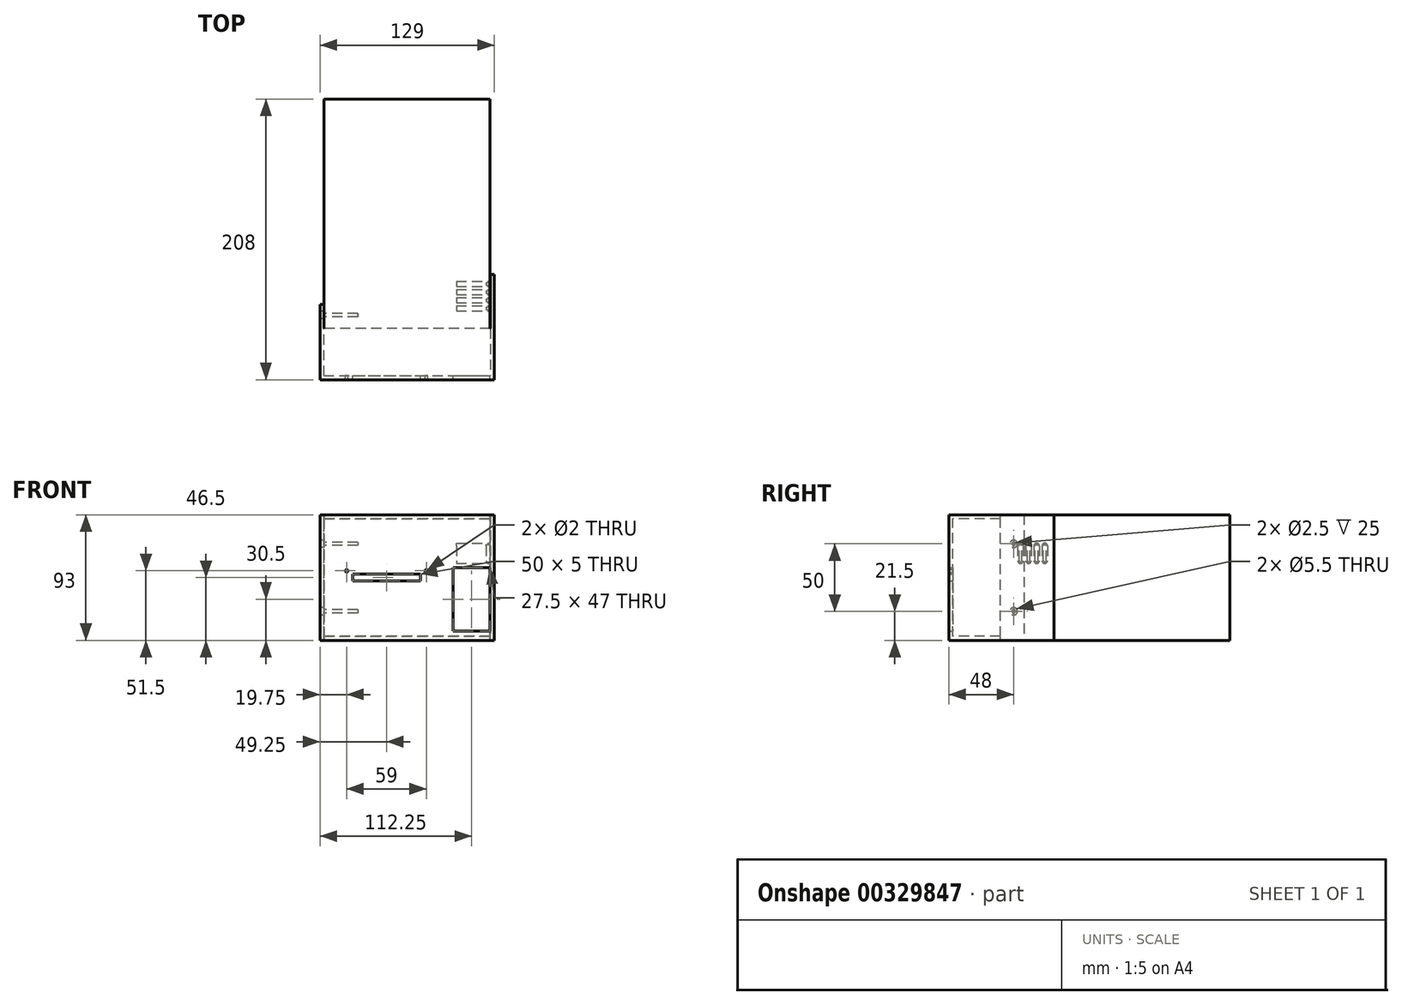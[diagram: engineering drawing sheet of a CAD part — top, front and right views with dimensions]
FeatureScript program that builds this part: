
annotation { "Feature Type Name" : "Feature", "Feature Type Description" : "" }
export const myFeature = defineFeature(function(context is Context, id is Id, definition is map)
    precondition{}
    {
        {
            assignVariable(context, id + "F0", {"name" : "CoverWallThickness", "anyValue" : 3});
        }
        {
            assignVariable(context, id + "F1", {"name" : "Gap", "anyValue" : 0.2});
        }
        {
            var Q0;
            Q0=qCreatedBy(makeId("Front.planeOp"),FACE);
            var sketch = newSketch(context, id + "F2", { "sketchPlane" : qUnion([Q0])});
            skLineSegment(sketch, "E0.bottom", {"start": v(0, 0) * mm, "end": v(123, 0) * mm});
            skLineSegment(sketch, "E0.top", {"start": v(0, 93) * mm, "end": v(123, 93) * mm});
            skLineSegment(sketch, "E0.left", {"start": v(0, 0) * mm, "end": v(0, 93) * mm});
            skLineSegment(sketch, "E0.right", {"start": v(123, 0) * mm, "end": v(123, 93) * mm});
            skSolve(sketch);
        }
        {
            var Q0;
            Q0=makeQuery(id+"F2.imprint","IMPRINT",FACE,{"disambiguationData":[TD([[makeQuery(id+"F2.imprint","IMPRINT",EDGE,{"derivedFrom":sQuery(id+"F2.wireOp",EDGE,"E0.bottom")}),1.0]])]});
            extrude(context, id + "F3", {"entities" : qUnion([Q0]), "depth" : 170 * mm, "offsetDistance" : 25 * mm});
        }
        {
            var Q0;
            Q0=makeQuery(id+"F3.opExtrude","SWEPT_FACE",FACE,{"disambiguationData":[OSD([sQuery(id+"F2.wireOp",EDGE,"E0.left")])]});
            var sketch = newSketch(context, id + "F4", { "sketchPlane" : qUnion([Q0])});
            skCircle(sketch, "E1", {"center": v(160, 71.5) * mm, "radius": 1.25 * mm});
            skCircle(sketch, "E2", {"center": v(160, 21.5) * mm, "radius": 1.25 * mm});
            skSolve(sketch);
        }
        {
            var Q0;
            Q0 = qSketchRegion(id + "F4", true);
            extrude(context, id + "F5", {"entities" : qUnion([Q0]), "operationType" : NewBodyOperationType.REMOVE, "oppositeDirection" : true, "depth" : 25 * mm, "offsetDistance" : 25 * mm});
        }
        {
            var Q0;
            Q0=makeQuery(id+"F3.opExtrude","SWEPT_FACE",FACE,{"disambiguationData":[OSD([sQuery(id+"F2.wireOp",EDGE,"E0.right")])]});
            var sketch = newSketch(context, id + "F6", { "sketchPlane" : qUnion([Q0])});
            skLineSegment(sketch, "E3", {"start": v(-157, 70) * mm, "end": v(-157, 59) * mm});
            skLineSegment(sketch, "E4", {"start": v(-153, 70) * mm, "end": v(-153, 59) * mm});
            skArc(sketch, "E5", {"start": v(-153, 70) * mm, "mid": v(-155, 72) * mm, "end": v(-157, 70) * mm});
            skArc(sketch, "E6", {"start": v(-157, 59) * mm, "mid": v(-155, 57) * mm, "end": v(-153, 59) * mm});
            skArc(sketch, "E7.1.0.0", {"start": v(-147, 70) * mm, "mid": v(-149, 72) * mm, "end": v(-151, 70) * mm});
            skLineSegment(sketch, "E7.1.0.1", {"start": v(-151, 70) * mm, "end": v(-151, 59) * mm});
            skArc(sketch, "E7.1.0.2", {"start": v(-151, 59) * mm, "mid": v(-149, 57) * mm, "end": v(-147, 59) * mm});
            skLineSegment(sketch, "E7.1.0.3", {"start": v(-147, 70) * mm, "end": v(-147, 59) * mm});
            skArc(sketch, "E7.2.0.0", {"start": v(-141, 70) * mm, "mid": v(-143, 72) * mm, "end": v(-145, 70) * mm});
            skLineSegment(sketch, "E7.2.0.1", {"start": v(-145, 70) * mm, "end": v(-145, 59) * mm});
            skArc(sketch, "E7.2.0.2", {"start": v(-145, 59) * mm, "mid": v(-143, 57) * mm, "end": v(-141, 59) * mm});
            skLineSegment(sketch, "E7.2.0.3", {"start": v(-141, 70) * mm, "end": v(-141, 59) * mm});
            skArc(sketch, "E7.3.0.0", {"start": v(-135, 70) * mm, "mid": v(-137, 72) * mm, "end": v(-139, 70) * mm});
            skLineSegment(sketch, "E7.3.0.1", {"start": v(-139, 70) * mm, "end": v(-139, 59) * mm});
            skArc(sketch, "E7.3.0.2", {"start": v(-139, 59) * mm, "mid": v(-137, 57) * mm, "end": v(-135, 59) * mm});
            skLineSegment(sketch, "E7.3.0.3", {"start": v(-135, 70) * mm, "end": v(-135, 59) * mm});
            skLineSegment(sketch, "E7.direction1", {"start": v(-157, 70) * mm, "end": v(-151, 70) * mm, "construction": true});
            skSolve(sketch);
        }
        {
            var Q0;
            Q0 = qSketchRegion(id + "F6", true);
            extrude(context, id + "F7", {"entities" : qUnion([Q0]), "operationType" : NewBodyOperationType.REMOVE, "oppositeDirection" : true, "depth" : 25 * mm, "offsetDistance" : 25 * mm});
        }
        {
            var Q0;
            Q0=makeQuery(id+"F3.opExtrude","CAP_FACE",FACE,{"disambiguationData":[OSD([sQuery(id+"F2.wireOp",EDGE,"E0.bottom"),sQuery(id+"F2.wireOp",EDGE,"E0.top"),sQuery(id+"F2.wireOp",EDGE,"E0.left"),sQuery(id+"F2.wireOp",EDGE,"E0.right")])],"isStart":false});
            cPlane(context, id + "F8", {"entities" : qUnion([Q0]), "cplaneType" : CPlaneType.OFFSET, "offset" : 35 * mm, "width" : 150 * mm, "height" : 150 * mm});
        }
        {
            var Q0;
            Q0=qCreatedBy(id+"F8.planeOp",FACE);
            var sketch = newSketch(context, id + "F9", { "sketchPlane" : qUnion([Q0])});
            skLineSegment(sketch, "E8.bottom", {"start": v(-3, 0) * mm, "end": v(126, 0) * mm});
            skLineSegment(sketch, "E8.top", {"start": v(-3, 93) * mm, "end": v(126, 93) * mm});
            skLineSegment(sketch, "E8.left", {"start": v(-3, 0) * mm, "end": v(-3, 93) * mm});
            skLineSegment(sketch, "E8.right", {"start": v(126, 0) * mm, "end": v(126, 93) * mm});
            skLineSegment(sketch, "E9.bottom", {"start": v(95.5, 54) * mm, "end": v(123, 54) * mm});
            skLineSegment(sketch, "E9.top", {"start": v(95.5, 7) * mm, "end": v(123, 7) * mm});
            skLineSegment(sketch, "E9.left", {"start": v(95.5, 54) * mm, "end": v(95.5, 7) * mm});
            skLineSegment(sketch, "E9.right", {"start": v(123, 54) * mm, "end": v(123, 7) * mm});
            skLineSegment(sketch, "E10", {"start": v(-3, 90) * mm, "end": v(126, 90) * mm});
            skLineSegment(sketch, "E11", {"start": v(-3, 3) * mm, "end": v(126, 3) * mm});
            skLineSegment(sketch, "E12.bottom", {"start": v(21.25, 49) * mm, "end": v(71.25, 49) * mm});
            skLineSegment(sketch, "E12.top", {"start": v(21.25, 44) * mm, "end": v(71.25, 44) * mm});
            skLineSegment(sketch, "E12.left", {"start": v(21.25, 49) * mm, "end": v(21.25, 44) * mm});
            skLineSegment(sketch, "E12.right", {"start": v(71.25, 49) * mm, "end": v(71.25, 44) * mm});
            skCircle(sketch, "E13", {"center": v(16.75, 51.5) * mm, "radius": 1 * mm});
            skLineSegment(sketch, "E14", {"start": v(46.25, 49) * mm, "end": v(46.25, 44) * mm, "construction": true});
            skCircle(sketch, "E15.MirrorC", {"center": v(75.75, 51.5) * mm, "radius": 1 * mm});
            skLineSegment(sketch, "E16", {"start": v(21.25, 46.5) * mm, "end": v(71.25, 46.5) * mm, "construction": true});
            skLineSegment(sketch, "E17", {"start": v(-3, 46.5) * mm, "end": v(21.25, 46.5) * mm, "construction": true});
            skLineSegment(sketch, "E18", {"start": v(95.5, 30.5) * mm, "end": v(-3, 30.5) * mm, "construction": true});
            skLineSegment(sketch, "E19", {"start": v(46.25, 44) * mm, "end": v(46.25, 30.5) * mm, "construction": true});
            skSolve(sketch);
        }
        {
            var Q0;
            Q0 = qSketchRegion(id + "F9", true);
            extrude(context, id + "F10", {"entities" : qUnion([Q0]), "depth" : (getVariable(context, 'CoverWallThickness')) * mm, "offsetDistance" : 25 * mm});
        }
        {
            var Q0;
            {var subQ0=sQuery(id+"F9.wireOp",EDGE,"E8.top");Q0=makeQuery(id+"F9.imprint","IMPRINT",FACE,{"disambiguationData":[TD([[makeQuery(id+"F9.imprint","IMPRINT",EDGE,{"derivedFrom":subQ0}),-1.0]])]});}
            var Q1;
            {var subQ0=sQuery(id+"F9.wireOp",EDGE,"E8.bottom");Q1=makeQuery(id+"F9.imprint","IMPRINT",FACE,{"disambiguationData":[TD([[makeQuery(id+"F9.imprint","IMPRINT",EDGE,{"derivedFrom":subQ0}),1.0]])]});}
            var Q2;
            Q2=makeQuery(id+"F3.opExtrude","CAP_FACE",FACE,{"disambiguationData":[OSD([sQuery(id+"F2.wireOp",EDGE,"E0.bottom"),sQuery(id+"F2.wireOp",EDGE,"E0.top"),sQuery(id+"F2.wireOp",EDGE,"E0.left"),sQuery(id+"F2.wireOp",EDGE,"E0.right")])],"isStart":false});
            extrude(context, id + "F11", {"entities" : qUnion([Q0, Q1]), "operationType" : NewBodyOperationType.ADD, "endBound" : BoundingType.UP_TO_SURFACE, "oppositeDirection" : true, "depth" : 25 * mm, "endBoundEntityFace" : qUnion([Q2]), "offsetDistance" : 25 * mm});
        }
        {
            var Q0;
            {var subQ0=sQuery(id+"F9.wireOp",EDGE,"E8.left");Q0=makeQuery(id+"F11.boolean.opBoolean","MERGE",FACE,{"derivedFrom":[makeQuery(id+"F10.opExtrude","SWEPT_FACE",FACE,{"disambiguationData":[OSD([subQ0])]}),makeQuery(id+"F11.opExtrude","SWEPT_FACE",FACE,{"disambiguationData":[OSD([subQ0]),TDD([makeQuery(id+"F9.imprint","IMPRINT",EDGE,{"disambiguationData":[TD([[makeQuery(id+"F9.imprint","INTERSECT",VERTEX,{"derivedFrom":[sQuery(id+"F9.wireOp",EDGE,"E8.bottom"),subQ0]}),-1.0]])],"derivedFrom":subQ0})])]}),makeQuery(id+"F11.opExtrude","SWEPT_FACE",FACE,{"disambiguationData":[OSD([subQ0]),TDD([makeQuery(id+"F9.imprint","IMPRINT",EDGE,{"disambiguationData":[TD([[makeQuery(id+"F9.imprint","INTERSECT",VERTEX,{"derivedFrom":[sQuery(id+"F9.wireOp",EDGE,"E8.top"),subQ0]}),1.0]])],"derivedFrom":subQ0})])]})]});}
            var sketch = newSketch(context, id + "F12", { "sketchPlane" : qUnion([Q0])});
            skLineSegment(sketch, "E20", {"start": v(208, 93) * mm, "end": v(170, 93) * mm});
            skLineSegment(sketch, "E21", {"start": v(170, 93) * mm, "end": v(170, 93) * mm});
            skLineSegment(sketch, "E22", {"start": v(170, 93) * mm, "end": v(152.25, 93) * mm});
            skLineSegment(sketch, "E23", {"start": v(152.25, 93) * mm, "end": v(152.25, 0) * mm});
            skLineSegment(sketch, "E24", {"start": v(152.25, 0) * mm, "end": v(208, 0) * mm});
            skCircle(sketch, "E25", {"center": v(160, 71.5) * mm, "radius": 2.75 * mm});
            skCircle(sketch, "E26", {"center": v(160, 21.5) * mm, "radius": 2.75 * mm});
            skLineSegment(sketch, "E27", {"start": v(208, 93) * mm, "end": v(208, 0) * mm});
            skSolve(sketch);
        }
        {
            var Q0;
            Q0=makeQuery(id+"F3.opExtrude","SWEPT_FACE",FACE,{"disambiguationData":[OSD([sQuery(id+"F2.wireOp",EDGE,"E0.left")])]});
            cPlane(context, id + "F13", {"entities" : qUnion([Q0]), "cplaneType" : CPlaneType.OFFSET, "offset" : (getVariable(context, 'Gap')) * mm, "width" : 150 * mm, "height" : 150 * mm});
        }
        {
            var Q0;
            Q0 = qSketchRegion(id + "F12", true);
            var Q1;
            Q1=qCreatedBy(id+"F13.planeOp",FACE);
            extrude(context, id + "F14", {"entities" : qUnion([Q0]), "operationType" : NewBodyOperationType.ADD, "endBound" : BoundingType.UP_TO_SURFACE, "oppositeDirection" : true, "depth" : 25 * mm, "endBoundEntityFace" : qUnion([Q1]), "offsetDistance" : 25 * mm});
        }
        {
            var Q0;
            {var subQ0=sQuery(id+"F9.wireOp",EDGE,"E8.right");Q0=makeQuery(id+"F11.boolean.opBoolean","MERGE",FACE,{"derivedFrom":[makeQuery(id+"F10.opExtrude","SWEPT_FACE",FACE,{"disambiguationData":[OSD([subQ0])]}),makeQuery(id+"F11.opExtrude","SWEPT_FACE",FACE,{"disambiguationData":[OSD([subQ0]),TDD([makeQuery(id+"F9.imprint","IMPRINT",EDGE,{"disambiguationData":[TD([[makeQuery(id+"F9.imprint","INTERSECT",VERTEX,{"derivedFrom":[sQuery(id+"F9.wireOp",EDGE,"E8.bottom"),subQ0]}),-1.0]])],"derivedFrom":subQ0})])]}),makeQuery(id+"F11.opExtrude","SWEPT_FACE",FACE,{"disambiguationData":[OSD([subQ0]),TDD([makeQuery(id+"F9.imprint","IMPRINT",EDGE,{"disambiguationData":[TD([[makeQuery(id+"F9.imprint","INTERSECT",VERTEX,{"derivedFrom":[sQuery(id+"F9.wireOp",EDGE,"E8.top"),subQ0]}),1.0]])],"derivedFrom":subQ0})])]})]});}
            var sketch = newSketch(context, id + "F15", { "sketchPlane" : qUnion([Q0])});
            skLineSegment(sketch, "E28", {"start": v(-208, 93) * mm, "end": v(-208, 0) * mm});
            skLineSegment(sketch, "E29", {"start": v(-208, 0) * mm, "end": v(-130, 0) * mm});
            skLineSegment(sketch, "E30", {"start": v(-130, 0) * mm, "end": v(-130, 93) * mm});
            skLineSegment(sketch, "E31", {"start": v(-130, 93) * mm, "end": v(-170, 93) * mm});
            skLineSegment(sketch, "E32", {"start": v(-170, 93) * mm, "end": v(-170, 93) * mm});
            skLineSegment(sketch, "E33", {"start": v(-170, 93) * mm, "end": v(-208, 93) * mm});
            skLineSegment(sketch, "E34.0", {"start": v(-156, 70) * mm, "end": v(-156, 59) * mm});
            skArc(sketch, "E34.1", {"start": v(-154, 70) * mm, "mid": v(-155, 71) * mm, "end": v(-156, 70) * mm});
            skLineSegment(sketch, "E34.2", {"start": v(-154, 70) * mm, "end": v(-154, 59) * mm});
            skArc(sketch, "E34.3", {"start": v(-156, 59) * mm, "mid": v(-155, 58) * mm, "end": v(-154, 59) * mm});
            skLineSegment(sketch, "E35.0", {"start": v(-150, 70) * mm, "end": v(-150, 59) * mm});
            skArc(sketch, "E35.1", {"start": v(-148, 70) * mm, "mid": v(-149, 71) * mm, "end": v(-150, 70) * mm});
            skLineSegment(sketch, "E35.2", {"start": v(-148, 70) * mm, "end": v(-148, 59) * mm});
            skArc(sketch, "E35.3", {"start": v(-150, 59) * mm, "mid": v(-149, 58) * mm, "end": v(-148, 59) * mm});
            skLineSegment(sketch, "E36.0", {"start": v(-144, 70) * mm, "end": v(-144, 59) * mm});
            skArc(sketch, "E36.1", {"start": v(-142, 70) * mm, "mid": v(-143, 71) * mm, "end": v(-144, 70) * mm});
            skLineSegment(sketch, "E36.2", {"start": v(-142, 70) * mm, "end": v(-142, 59) * mm});
            skArc(sketch, "E36.3", {"start": v(-144, 59) * mm, "mid": v(-143, 58) * mm, "end": v(-142, 59) * mm});
            skLineSegment(sketch, "E37.0", {"start": v(-138, 70) * mm, "end": v(-138, 59) * mm});
            skArc(sketch, "E37.1", {"start": v(-136, 70) * mm, "mid": v(-137, 71) * mm, "end": v(-138, 70) * mm});
            skLineSegment(sketch, "E37.2", {"start": v(-136, 70) * mm, "end": v(-136, 59) * mm});
            skArc(sketch, "E37.3", {"start": v(-138, 59) * mm, "mid": v(-137, 58) * mm, "end": v(-136, 59) * mm});
            skSolve(sketch);
        }
        {
            var Q0;
            Q0=makeQuery(id+"F3.opExtrude","SWEPT_FACE",FACE,{"disambiguationData":[OSD([sQuery(id+"F2.wireOp",EDGE,"E0.right")])]});
            cPlane(context, id + "F16", {"entities" : qUnion([Q0]), "cplaneType" : CPlaneType.OFFSET, "offset" : (getVariable(context, 'Gap')) * mm, "width" : 150 * mm, "height" : 150 * mm});
        }
        {
            var Q0;
            Q0 = qSketchRegion(id + "F15", true);
            var Q1;
            Q1=qCreatedBy(id+"F16.planeOp",FACE);
            extrude(context, id + "F17", {"entities" : qUnion([Q0]), "operationType" : NewBodyOperationType.ADD, "endBound" : BoundingType.UP_TO_SURFACE, "oppositeDirection" : true, "depth" : 25 * mm, "endBoundEntityFace" : qUnion([Q1]), "offsetDistance" : 25 * mm});
        }
        {
            var Q0;
            Q0=makeQuery(id+"F15.imprint","IMPRINT",FACE,{"disambiguationData":[TD([[makeQuery(id+"F15.imprint","IMPRINT",EDGE,{"derivedFrom":sQuery(id+"F15.wireOp",EDGE,"E34.0")}),1.0]])]});
            var Q1;
            Q1=makeQuery(id+"F15.imprint","IMPRINT",FACE,{"disambiguationData":[TD([[makeQuery(id+"F15.imprint","IMPRINT",EDGE,{"derivedFrom":sQuery(id+"F15.wireOp",EDGE,"E35.0")}),1.0]])]});
            var Q2;
            Q2=makeQuery(id+"F15.imprint","IMPRINT",FACE,{"disambiguationData":[TD([[makeQuery(id+"F15.imprint","IMPRINT",EDGE,{"derivedFrom":sQuery(id+"F15.wireOp",EDGE,"E36.0")}),1.0]])]});
            var Q3;
            Q3=makeQuery(id+"F15.imprint","IMPRINT",FACE,{"disambiguationData":[TD([[makeQuery(id+"F15.imprint","IMPRINT",EDGE,{"derivedFrom":sQuery(id+"F15.wireOp",EDGE,"E37.0")}),1.0]])]});
            extrude(context, id + "F18", {"entities" : qUnion([Q0, Q1, Q2, Q3]), "operationType" : NewBodyOperationType.ADD, "oppositeDirection" : true, "depth" : 6 * mm, "offsetDistance" : 25 * mm});
        }
    });
